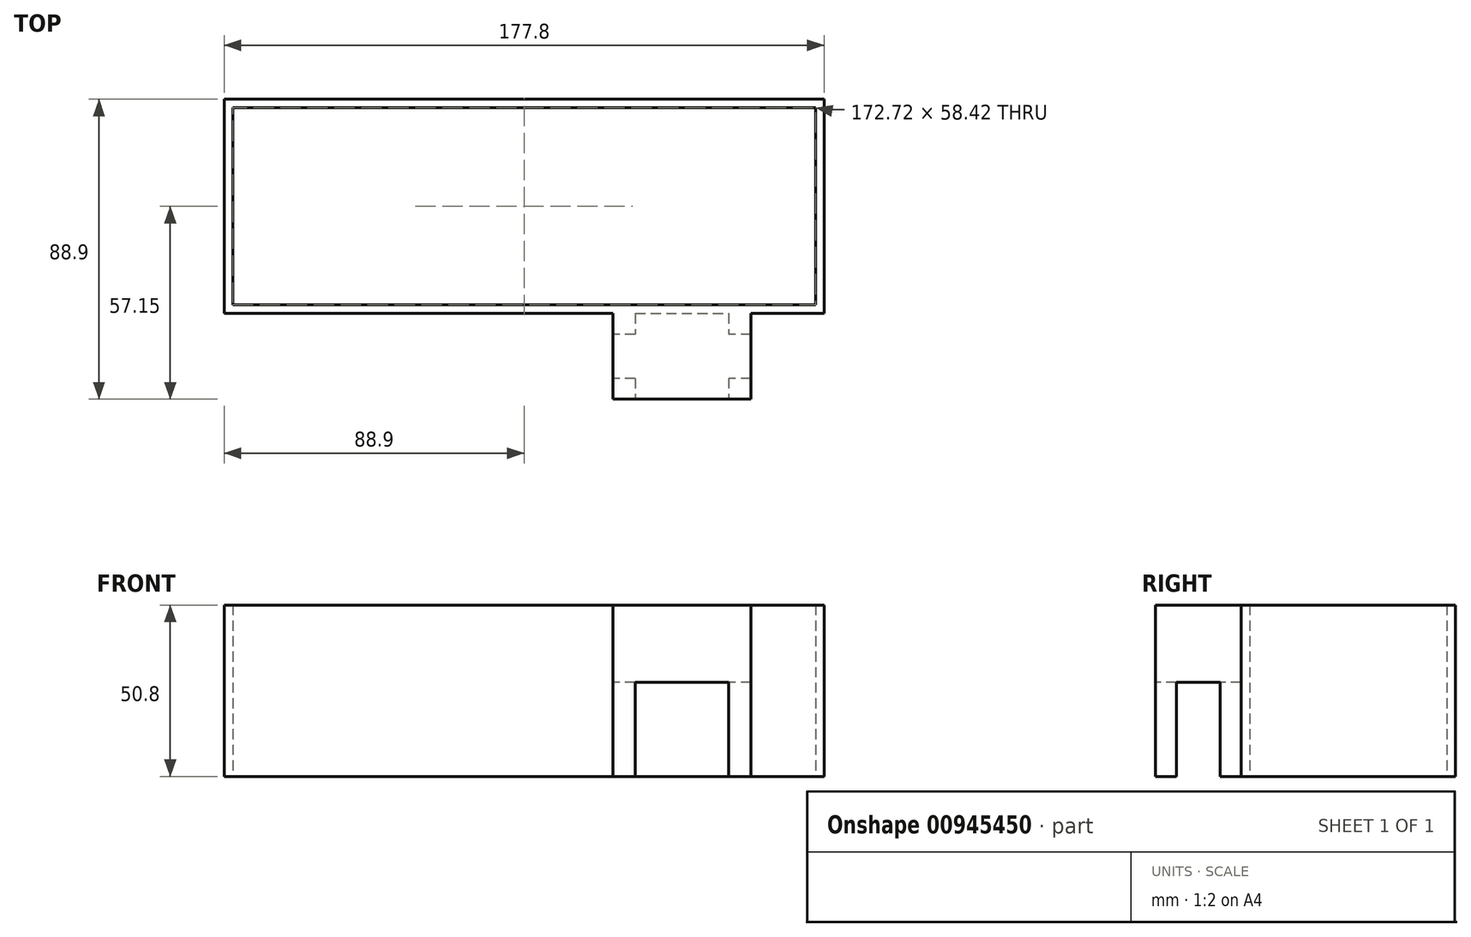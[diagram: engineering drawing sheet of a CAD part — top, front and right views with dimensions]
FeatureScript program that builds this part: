
annotation { "Feature Type Name" : "Feature", "Feature Type Description" : "" }
export const myFeature = defineFeature(function(context is Context, id is Id, definition is map)
    precondition{}
    {
        {
            var Q0;
            Q0=qCreatedBy(makeId("Top.planeOp"),FACE);
            var sketch = newSketch(context, id + "F0", { "sketchPlane" : qUnion([Q0])});
            skLineSegment(sketch, "E0.bottom", {"start": v(-88.9, -31.75) * mm, "end": v(88.9, -31.75) * mm});
            skLineSegment(sketch, "E0.top", {"start": v(-88.9, 31.75) * mm, "end": v(88.9, 31.75) * mm});
            skLineSegment(sketch, "E0.left", {"start": v(-88.9, -31.75) * mm, "end": v(-88.9, 31.75) * mm});
            skLineSegment(sketch, "E0.right", {"start": v(88.9, -31.75) * mm, "end": v(88.9, 31.75) * mm});
            skPoint(sketch, "E0.middle", {"position": v(0, 0) * mm});
            skSolve(sketch);
        }
        {
            var Q0;
            Q0=makeQuery(id+"F0.imprint","IMPRINT",FACE,{"disambiguationData":[TD([[makeQuery(id+"F0.imprint","IMPRINT",EDGE,{"derivedFrom":sQuery(id+"F0.wireOp",EDGE,"E0.bottom")}),1.0]])]});
            extrude(context, id + "F1", {"entities" : qUnion([Q0]), "depth" : 50.8 * mm, "offsetDistance" : 25.4 * mm});
        }
        {
            var Q0;
            Q0=makeQuery(id+"F1.opExtrude","SWEPT_FACE",FACE,{"disambiguationData":[OSD([sQuery(id+"F0.wireOp",EDGE,"E0.bottom")])]});
            var sketch = newSketch(context, id + "F2", { "sketchPlane" : qUnion([Q0])});
            skLineSegment(sketch, "E1.bottom", {"start": v(67.23, 0) * mm, "end": v(26.32, 0) * mm});
            skLineSegment(sketch, "E1.top", {"start": v(67.23, 50.8) * mm, "end": v(26.32, 50.8) * mm});
            skLineSegment(sketch, "E1.left", {"start": v(67.23, 0) * mm, "end": v(67.23, 50.8) * mm});
            skLineSegment(sketch, "E1.right", {"start": v(26.32, 0) * mm, "end": v(26.32, 50.8) * mm});
            skPoint(sketch, "E1.middle", {"position": v(46.77, 25.4) * mm});
            skPoint(sketch, "E1.middle.positionSnap0", {"position": v(88.9, 25.4) * mm});
            skPoint(sketch, "E1.centerSnap0", {"position": v(88.9, 25.4) * mm});
            skSolve(sketch);
        }
        {
            var Q0;
            Q0 = qSketchRegion(id + "F2", true);
            extrude(context, id + "F3", {"entities" : qUnion([Q0]), "operationType" : NewBodyOperationType.ADD, "depth" : 25.4 * mm, "offsetDistance" : 25.4 * mm});
        }
        {
            var Q0;
            Q0=makeQuery(id+"F3.opExtrude","CAP_FACE",FACE,{"disambiguationData":[OSD([sQuery(id+"F2.wireOp",EDGE,"E1.bottom"),sQuery(id+"F2.wireOp",EDGE,"E1.top"),sQuery(id+"F2.wireOp",EDGE,"E1.left"),sQuery(id+"F2.wireOp",EDGE,"E1.right")])],"isStart":false});
            var sketch = newSketch(context, id + "F4", { "sketchPlane" : qUnion([Q0])});
            skLineSegment(sketch, "E2.bottom", {"start": v(32.94, 0) * mm, "end": v(60.6, 0) * mm});
            skLineSegment(sketch, "E2.top", {"start": v(32.94, 27.94) * mm, "end": v(60.6, 27.94) * mm});
            skLineSegment(sketch, "E2.left", {"start": v(32.94, 0) * mm, "end": v(32.94, 27.94) * mm});
            skLineSegment(sketch, "E2.right", {"start": v(60.6, 0) * mm, "end": v(60.6, 27.94) * mm});
            skPoint(sketch, "E2.middle", {"position": v(46.77, 13.97) * mm});
            skPoint(sketch, "E2.middle.positionSnap0", {"position": v(46.77, 0) * mm});
            skPoint(sketch, "E2.centerSnap0", {"position": v(46.77, 0) * mm});
            skSolve(sketch);
        }
        {
            var Q0;
            Q0 = qSketchRegion(id + "F4", true);
            extrude(context, id + "F5", {"entities" : qUnion([Q0]), "operationType" : NewBodyOperationType.REMOVE, "oppositeDirection" : true, "depth" : 25.4 * mm, "offsetDistance" : 25.4 * mm});
        }
        {
            var Q0;
            Q0=makeQuery(id+"F3.opExtrude","SWEPT_FACE",FACE,{"disambiguationData":[OSD([sQuery(id+"F2.wireOp",EDGE,"E1.right")])]});
            var sketch = newSketch(context, id + "F6", { "sketchPlane" : qUnion([Q0])});
            skLineSegment(sketch, "E3.bottom", {"start": v(37.94, 0) * mm, "end": v(50.96, 0) * mm});
            skLineSegment(sketch, "E3.top", {"start": v(37.94, 27.94) * mm, "end": v(50.96, 27.94) * mm});
            skLineSegment(sketch, "E3.left", {"start": v(37.94, 0) * mm, "end": v(37.94, 27.94) * mm});
            skLineSegment(sketch, "E3.right", {"start": v(50.96, 0) * mm, "end": v(50.96, 27.94) * mm});
            skPoint(sketch, "E3.middle", {"position": v(44.45, 13.97) * mm});
            skPoint(sketch, "E3.middle.positionSnap0", {"position": v(44.45, 50.8) * mm});
            skPoint(sketch, "E3.centerSnap0", {"position": v(44.45, 50.8) * mm});
            skSolve(sketch);
        }
        {
            var Q0;
            Q0 = qSketchRegion(id + "F6", true);
            extrude(context, id + "F7", {"entities" : qUnion([Q0]), "operationType" : NewBodyOperationType.REMOVE, "oppositeDirection" : true, "depth" : 45.47 * mm, "offsetDistance" : 25.4 * mm});
        }
        {
            var Q0;
            {var subQ0=sQuery(id+"F0.wireOp",EDGE,"E0.left");var subQ1=sQuery(id+"F0.wireOp",EDGE,"E0.top");var subQ2=sQuery(id+"F0.wireOp",EDGE,"E0.right");var subQ3=sQuery(id+"F0.wireOp",EDGE,"E0.bottom");var subQ4=sQuery(id+"F4.wireOp",EDGE,"E2.right");var subQ5=sQuery(id+"F4.wireOp",EDGE,"E2.left");Q0=makeQuery(id+"F7.boolean.opBoolean","SPLIT",FACE,{"disambiguationData":[TD([makeQuery(id+"F1.opExtrude","SWEPT_FACE",FACE,{"disambiguationData":[OSD([subQ3])]}),makeQuery(id+"F1.opExtrude","SWEPT_FACE",FACE,{"disambiguationData":[OSD([subQ1])]}),makeQuery(id+"F1.opExtrude","SWEPT_FACE",FACE,{"disambiguationData":[OSD([subQ0])]}),makeQuery(id+"F1.opExtrude","SWEPT_FACE",FACE,{"disambiguationData":[OSD([subQ2])]}),makeQuery(id+"F3.opExtrude","SWEPT_FACE",FACE,{"disambiguationData":[OSD([sQuery(id+"F2.wireOp",EDGE,"E1.left")])]}),makeQuery(id+"F3.opExtrude","SWEPT_FACE",FACE,{"disambiguationData":[OSD([sQuery(id+"F2.wireOp",EDGE,"E1.right")])]}),makeQuery(id+"F5.boolean.opBoolean","COPY",FACE,{"derivedFrom":makeQuery(id+"F5.opExtrude","CAP_FACE",FACE,{"disambiguationData":[OSD([sQuery(id+"F4.wireOp",EDGE,"E2.bottom"),sQuery(id+"F4.wireOp",EDGE,"E2.top"),subQ5,subQ4])],"isStart":false})}),makeQuery(id+"F5.boolean.opBoolean","COPY",FACE,{"derivedFrom":makeQuery(id+"F5.opExtrude","SWEPT_FACE",FACE,{"disambiguationData":[OSD([subQ5])]})}),makeQuery(id+"F5.boolean.opBoolean","COPY",FACE,{"derivedFrom":makeQuery(id+"F5.opExtrude","SWEPT_FACE",FACE,{"disambiguationData":[OSD([subQ4])]})}),makeQuery(id+"F7.opExtrude","SWEPT_FACE",FACE,{"disambiguationData":[OSD([sQuery(id+"F6.wireOp",EDGE,"E3.left")])]})])],"derivedFrom":makeQuery(id+"F3.boolean.opBoolean","MERGE",FACE,{"derivedFrom":[makeQuery(id+"F1.opExtrude","CAP_FACE",FACE,{"disambiguationData":[OSD([subQ3,subQ1,subQ0,subQ2])],"isStart":true}),makeQuery(id+"F3.opExtrude","SWEPT_FACE",FACE,{"disambiguationData":[OSD([sQuery(id+"F2.wireOp",EDGE,"E1.bottom")])]})]})});}
            var sketch = newSketch(context, id + "F8", { "sketchPlane" : qUnion([Q0])});
            skLineSegment(sketch, "E4.bottom", {"start": v(-86.36, -29.21) * mm, "end": v(86.36, -29.21) * mm});
            skLineSegment(sketch, "E4.top", {"start": v(-86.36, 29.21) * mm, "end": v(86.36, 29.21) * mm});
            skLineSegment(sketch, "E4.left", {"start": v(-86.36, -29.21) * mm, "end": v(-86.36, 29.21) * mm});
            skLineSegment(sketch, "E4.right", {"start": v(86.36, -29.21) * mm, "end": v(86.36, 29.21) * mm});
            skPoint(sketch, "E4.middle", {"position": v(0, 0) * mm});
            skSolve(sketch);
        }
        {
            var Q0;
            Q0 = qSketchRegion(id + "F8", true);
            extrude(context, id + "F9", {"entities" : qUnion([Q0]), "operationType" : NewBodyOperationType.REMOVE, "oppositeDirection" : true, "depth" : 74.93 * mm, "offsetDistance" : 25.4 * mm});
        }
    });
